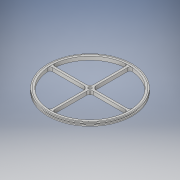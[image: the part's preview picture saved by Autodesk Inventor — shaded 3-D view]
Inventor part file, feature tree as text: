
AUTODESK INVENTOR PART (.ipt)
format: ipt  version: 2018 (Build 220112000, 112)  size: 219,136 bytes
history: native  units: in
note: dims shown in document units (in); Inventor stores cm internally (conversion verified against a paired STEP export)
features: extrude x7, sketch x7, fillet x2
ambient origin geometry x8: Origin, YZ Plane, XZ Plane, XY Plane, X Axis, Y Axis, Z Axis, Center Point
bodies: Solid1 (feature_tree)
feature tree (16):
  extrude  "Extrusion1"  Depth=4.849in
  extrude  "Extrusion2"  Depth=0.0625in
  extrude  "Extrusion3"  Depth=0.0625in TaperAngle=0.0deg
  extrude  "Extrusion4"  Depth=0.204in
  extrude  "Extrusion5"  Depth=0.204in
  extrude  "Extrusion6"  Depth=0.125in
  extrude  "Extrusion7"  Depth=0.204in TaperAngle=0.0deg
  fillet  "Fillet1"  Radius=0.125in
  fillet  "Fillet2"  Radius=0.125in
  sketch  "Sketch1"  dims[d0=4.7244in d1=4.849in]
  sketch  "Sketch2"  dims[d2=0.0625in d3=0.0in d4=4.5in]
  sketch  "Sketch3"  dims[d5=0.0787in d6=0.0in d7=0.0625in d8=0.0in]
  sketch  "Sketch4"  dims[d9=0.204in d10=0.0in d11=4.5in]
  sketch  "Sketch5"  dims[d12=0.204in d13=0.0in d14=0.195in]
  sketch  "Sketch6"  dims[d15=0.204in d16=0.0in d17=0.125in]
  sketch  "Sketch7"  dims[d18=0.125in d19=0.204in d20=0.0in d21=0.125in d22=0.125in]
